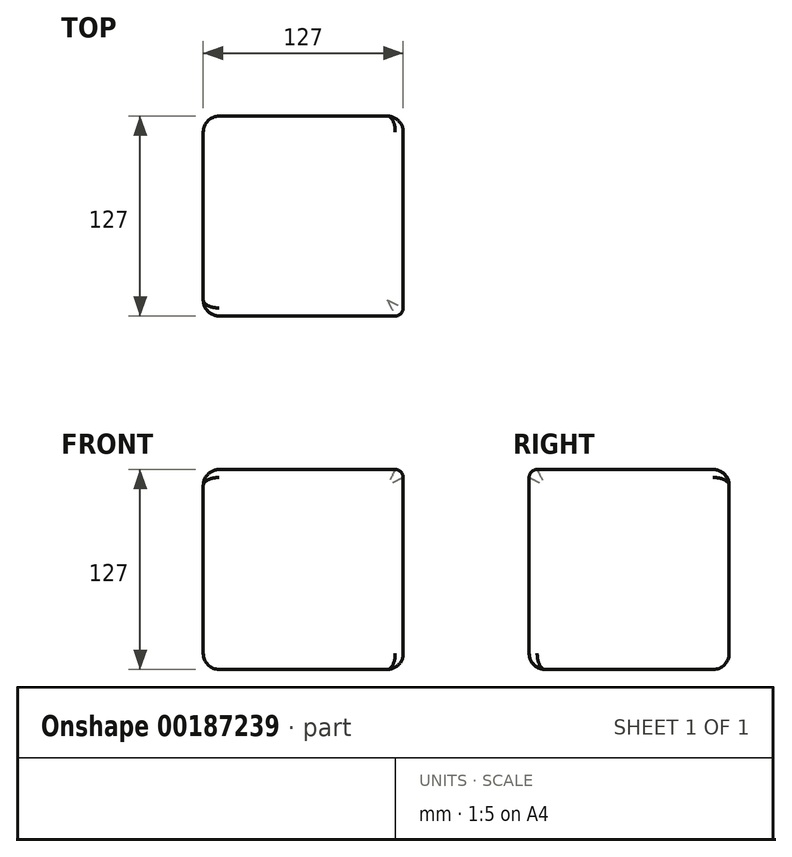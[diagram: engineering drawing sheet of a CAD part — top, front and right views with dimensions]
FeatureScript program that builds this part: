
annotation { "Feature Type Name" : "Feature", "Feature Type Description" : "" }
export const myFeature = defineFeature(function(context is Context, id is Id, definition is map)
    precondition{}
    {
        {
            var Q0;
            Q0=qCreatedBy(makeId("Top.planeOp"),FACE);
            var sketch = newSketch(context, id + "F0", { "sketchPlane" : qUnion([Q0])});
            skLineSegment(sketch, "E0.bottom", {"start": v(-74.03, 63.72) * mm, "end": v(52.97, 63.72) * mm});
            skLineSegment(sketch, "E0.top", {"start": v(-74.03, -63.28) * mm, "end": v(52.97, -63.28) * mm});
            skLineSegment(sketch, "E0.left", {"start": v(-74.03, 63.72) * mm, "end": v(-74.03, -63.28) * mm});
            skLineSegment(sketch, "E0.right", {"start": v(52.97, 63.72) * mm, "end": v(52.97, -63.28) * mm});
            skSolve(sketch);
        }
        {
            var Q0;
            Q0=makeQuery(id+"F0.imprint","IMPRINT",FACE,{"disambiguationData":[TD([[makeQuery(id+"F0.imprint","IMPRINT",EDGE,{"derivedFrom":sQuery(id+"F0.wireOp",EDGE,"E0.bottom")}),-1.0]])]});
            extrude(context, id + "F1", {"entities" : qUnion([Q0]), "depth" : 127 * mm});
        }
        {
            var Q0;
            Q0=makeQuery(id+"F1.opExtrude","CAP_EDGE",EDGE,{"disambiguationData":[OSD([sQuery(id+"F0.wireOp",EDGE,"E0.top")])],"isStart":false});
            fillet(context, id + "F2", {"entities" : qUnion([Q0]), "radius" : 5.08 * mm, "tangentPropagation" : true, "allowEdgeOverflow" : false});
        }
        {
            var Q0;
            Q0=makeQuery(id+"F1.opExtrude","SWEPT_EDGE",EDGE,{"disambiguationData":[OSD([sQuery(id+"F0.wireOp",EDGE,"E0.top"),sQuery(id+"F0.wireOp",EDGE,"E0.right")])]});
            fillet(context, id + "F3", {"entities" : qUnion([Q0]), "radius" : 5.08 * mm, "tangentPropagation" : true, "allowEdgeOverflow" : false});
        }
        {
            var Q0;
            Q0=makeQuery(id+"F1.opExtrude","SWEPT_EDGE",EDGE,{"disambiguationData":[OSD([sQuery(id+"F0.wireOp",EDGE,"E0.bottom"),sQuery(id+"F0.wireOp",EDGE,"E0.right")])]});
            var Q1;
            Q1=makeQuery(id+"F1.opExtrude","SWEPT_EDGE",EDGE,{"disambiguationData":[OSD([sQuery(id+"F0.wireOp",EDGE,"E0.bottom"),sQuery(id+"F0.wireOp",EDGE,"E0.left")])]});
            var Q2;
            Q2=makeQuery(id+"F1.opExtrude","CAP_EDGE",EDGE,{"disambiguationData":[OSD([sQuery(id+"F0.wireOp",EDGE,"E0.left")])],"isStart":false});
            var Q3;
            Q3=makeQuery(id+"F1.opExtrude","CAP_EDGE",EDGE,{"disambiguationData":[OSD([sQuery(id+"F0.wireOp",EDGE,"E0.left")])],"isStart":true});
            var Q4;
            Q4=makeQuery(id+"F1.opExtrude","CAP_EDGE",EDGE,{"disambiguationData":[OSD([sQuery(id+"F0.wireOp",EDGE,"E0.top")])],"isStart":true});
            var Q5;
            Q5=makeQuery(id+"F1.opExtrude","CAP_EDGE",EDGE,{"disambiguationData":[OSD([sQuery(id+"F0.wireOp",EDGE,"E0.bottom")])],"isStart":true});
            fillet(context, id + "F4", {"entities" : qUnion([Q0, Q1, Q2, Q3, Q4, Q5]), "radius" : 10.16 * mm, "tangentPropagation" : true, "allowEdgeOverflow" : false});
        }
    });
